# Revit family: IS_Septa_R0128_BIM_DE
name_source: partatom
category: Plumbing Fixtures
revit_build: Autodesk Revit 2017 (Build: 20160225_1515(x64)
units: mm (PartAtom-declared; Revit-internal decimal feet)

## family parameters
Cut with Voids When Loaded = No
Host = Face
OmniClass Number = 23.45.05.21.11.11
OmniClass Title = Water Operated Water Closets
Part Type = Normal
Room Calculation Point = No
Round Connector Dimension = Use Diameter
Shared = Yes

## types (1)
- R0128MY - SEPTA PRO M2 S/STEEL - IS
    Afmetingen = 243 x 18 x 163mm
    AfstandsEenheid = millimeters
    Afwerking = Chrome
    Artikelnummer = R0128MY
    Artikelomschrijving = Betätigungsplatte E1 SEPTA PRO, elektronischen Auslösung, Chrom
    Artikelreferentie = 1
    Assembly Code = C1030200
    Auteur = Ideal Standrad
    BREEAMApproved = No
    Barcode = 3391500580527
    Beschrijvinggarantie = Manufacturers Warranty
    BimObjectNaam = IS_Ideal Standard_WC cistern fittings_Septa_R0128MY
    Breedte = 0
    BrutoGewicht = 0
    CWFU = 0
    Cost = 0 $
    Default Elevation = 900 mm  [stored 2.95276 ft]
    Description = AntiVandal plate, CP - SF
    Diepte = 0 mm  [stored 0 ft]
    Douchebak = No
    DuurEenheid = year
    ECA = No
    Flush Plate Material = Stainless Steel, Brushed
    Garantieunits = Year
    GrootteAfvoergat = 0
    HWFU = 0
    Heefthandvaten = No
    Hulp = https://www.idealstandard.de
    Installatieinstructies = https://www.idealstandard.de
    Kleur = Chrome
    Lengte = 0 mm  [stored 0 ft]
    Materiaal = Metal
    Merk = Ideal Standard
    Model = R0128MY
    Montageinstuctie = https://www.idealstandard.de
    NBSDescription = WC cistern fittings
    NBSReference = 45-30-70/387
    Nettogewicht = 1.0224
    Overloop = 0 mm  [stored 0 ft]
    Productinformatie = https://www.idealstandard.de
    Telefoonnummer = +49 (0) 6571 16 0
    URL = https://www.idealstandard.de
    Uniclass2 = Pr_40_20_93_89
    Uniclass2015Description = Urinal and WC fittings
    Uniclass2015Referentie = Pr_40_20_93
    Urlproducent = https://www.idealstandard.de
    Versie = 1
    Vervangingskosten = 0
    Verwachtelevensduur = 5
    Volumeunits = Litres
    WFU = 0
    WRAS = No
    WaterEfficientProduct = No

note: [stored X ft] marks values corroborated as IEEE doubles in the binary element streams (Revit-internal decimal feet)

## geometry (parser evidence)
native form markers: Sweep x3
no freeform markers — native parametric forms only
